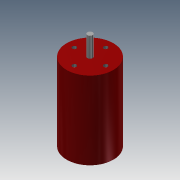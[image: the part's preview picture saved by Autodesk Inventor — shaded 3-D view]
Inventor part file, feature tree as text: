
AUTODESK INVENTOR PART (.ipt)
format: ipt  version: 2013 (Build 170138000, 138)  size: 95,744 bytes
history: native  units: mm
features: sketch x3, extrude x2, hole x1
ambient origin geometry x8: Origin, YZ Plane, XZ Plane, XY Plane, X Axis, Y Axis, Z Axis, Center Point
bodies: Solid1 (feature_tree)
feature tree (6):
  extrude  "Extrusion1"  Depth=47.0mm TaperAngle=0.0deg
  extrude  "Extrusion2"  Depth=12.0mm TaperAngle=0.0deg
  hole  "Hole1"  [1 undecoded]
  sketch  "Sketch1"  dims[d0=28.2mm d1=47.0mm d2=0.0mm]
  sketch  "Sketch2"  dims[d3=3.17mm d4=12.0mm d5=0.0mm]
  sketch  "Sketch3"  dims[d8=2.4mm d9=2.4mm d10=2.4mm d11=2.4mm d12=2.459mm d13=3.0mm d14=4.0mm d15=2.0mm d16=90.0deg d17=3.0mm d18=0.0mm]
note: 1 required parameter value undecoded (feature->parameter linkage not recoverable at this tier; creation-order binding heuristic only, values carry confidence <= 0.55)
